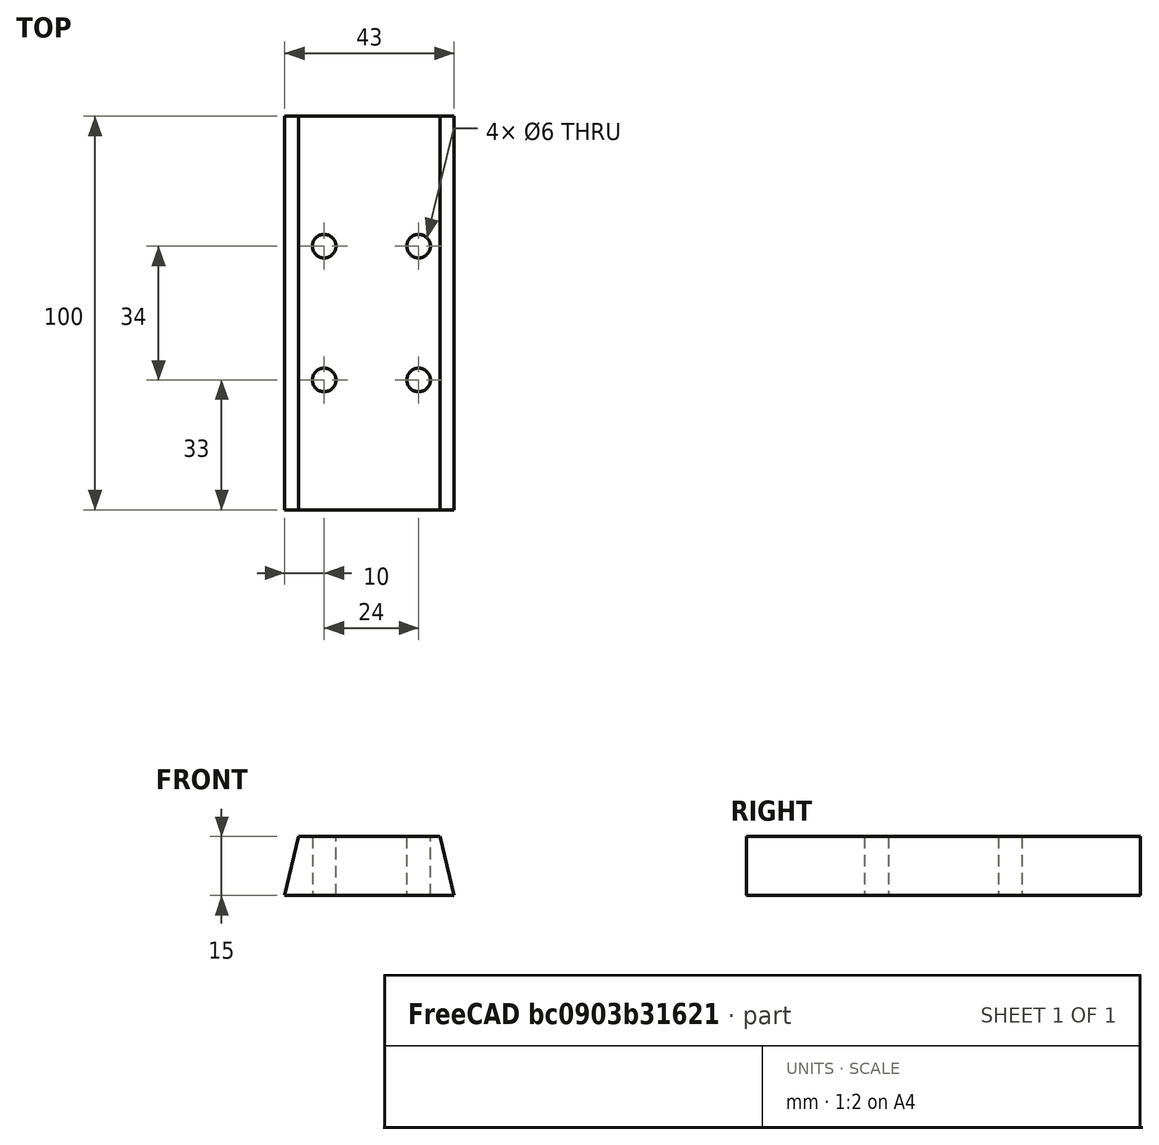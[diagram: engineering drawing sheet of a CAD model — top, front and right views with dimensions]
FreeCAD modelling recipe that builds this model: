
FCSTD DOCUMENT  (FreeCAD 1.0R38641 +678 (Git))
Label: lista k radiu
License: All rights reserved
LicenseURL: https://en.wikipedia.org/wiki/All_rights_reserved
objects: TechDraw::DrawViewDimension×9, Part::Cylinder×4, TechDraw::DrawProjGroupItem×3, Sketcher::SketchObject×1, Part::Extrusion×1, Part::MultiFuse×1, Part::Cut×1, TechDraw::DrawSVGTemplate×1, TechDraw::DrawProjGroup×1, TechDraw::DrawPage×1
note: 22 computed .brp shape members not serialized (recipe doc carries the construction recipe); baked Part::Feature solids carry a one-line shape summary decoded from their .brp

FEATURE [Sketcher::SketchObject] Sketch
  ArcFitTolerance = 1e-06
  FullyConstrained = true
  MakeInternals = false
  Placement = pos=(0,0,0) rot=(1,0,0;1.5708rad)
  sketch-geometry (4):
    g0: LineSegment StartX=0 StartY=0 StartZ=0 EndX=43 EndY=0 EndZ=0
    g1: LineSegment StartX=43 StartY=0 StartZ=0 EndX=39.5 EndY=15 EndZ=0
    g2: LineSegment StartX=39.5 StartY=15 StartZ=0 EndX=3.5 EndY=15 EndZ=0
    g3: LineSegment StartX=3.5 StartY=15 StartZ=0 EndX=0 EndY=0 EndZ=0
  constraints (11):
    c: Coincident(g-1,g0)
    c: PointOnObject(g0,g-1)
    c: Coincident(g0,g1)
    c: Coincident(g1,g2)
    c: Horizontal(g2)
    c: Coincident(g2,g3)
    c: Coincident(g3,g0)
    c: DistanceX(g0,g0) = 43
    c: DistanceX(g2,g2) = 36
    c: DistanceY(g3,g3) = 15
    c: DistanceX(g0,g2) = 3.5
FEATURE [Part::Extrusion] Extrude
  Base = -> Sketch
  Dir = (0,-1,2e-16)
  DirMode = 2
  FaceMakerClass = Part::FaceMakerBullseye
  FaceMakerMode = 3
  LengthFwd = 100
  LengthRev = 0
  Solid = true
  Symmetric = false
FEATURE [Part::Cylinder] Cylinder  label="Válec"
  Angle = 360
  AttacherType = Attacher::AttachEngine3D
  FirstAngle = 0
  Height = 20
  Radius = 3
  SecondAngle = 0
FEATURE [Part::Cylinder] Cylinder001  label="Válec001"
  Angle = 360
  AttacherType = Attacher::AttachEngine3D
  FirstAngle = 0
  Height = 20
  Placement = pos=(0,34,0) rot=(0,1,0;0rad)
  Radius = 3
  SecondAngle = 0
FEATURE [Part::Cylinder] Cylinder002  label="Válec002"
  Angle = 360
  AttacherType = Attacher::AttachEngine3D
  FirstAngle = 0
  Height = 20
  Placement = pos=(24,34,0) rot=(1,1,0;0rad)
  Radius = 3
  SecondAngle = 0
FEATURE [Part::Cylinder] Cylinder003  label="Válec003"
  Angle = 360
  AttacherType = Attacher::AttachEngine3D
  FirstAngle = 0
  Height = 20
  Placement = pos=(24,0,0) rot=(1,0,0;0rad)
  Radius = 3
  SecondAngle = 0
FEATURE [Part::MultiFuse] Fusion
  Placement = pos=(10,-67,0) rot=(1,1,0;0rad)
  Refine = true
  Shapes = -> [Cylinder,Cylinder001,Cylinder002,Cylinder003]
FEATURE [Part::Cut] Cut
  Base = -> Extrude
  Refine = true
  Tool = -> Fusion
FEATURE [TechDraw::DrawSVGTemplate] Template  label="Šablona"
  Height = 210
  Orientation = 1
  Template = /snap/freecad/1634/usr/share/Mod/TechDraw/Templates/Default_Template_A4_Landscape.svg
  Width = 297
FEATURE [TechDraw::DrawProjGroupItem] View  label="Front"
  CoarseView = false
  Direction = (0,-1,0)
  Focus = 100
  HardHidden = false
  IsoCount = 0
  IsoHidden = false
  IsoVisible = false
  LockPosition = true
  Perspective = false
  Rotation = 0
  RotationVector = (1,0,0)
  ScaleType = 2
  ScrubCount = 1
  SeamHidden = false
  SeamVisible = false
  SmoothHidden = false
  SmoothVisible = true
  Source = -> [Cut]
  Type = 0
  X = 0
  XDirection = (1,0,0)
  Y = 0
FEATURE [TechDraw::DrawProjGroupItem] ProjItem001  label="Horní"
  CoarseView = false
  Direction = (0,0,1)
  Focus = 100
  HardHidden = false
  IsoCount = 0
  IsoHidden = false
  IsoVisible = false
  LockPosition = false
  Perspective = false
  Rotation = 0
  RotationVector = (1,0,0)
  ScaleType = 0
  ScrubCount = 1
  SeamHidden = false
  SeamVisible = false
  SmoothHidden = false
  SmoothVisible = true
  Source = -> [Cut]
  Type = 4
  X = 0
  XDirection = (1,0,0)
  Y = -72.5
FEATURE [TechDraw::DrawProjGroupItem] ProjItem  label="FrontTopLeft"
  CoarseView = false
  Direction = (-0.57735,-0.57735,0.57735)
  Focus = 100
  HardHidden = false
  IsoCount = 0
  IsoHidden = false
  IsoVisible = false
  LockPosition = false
  Perspective = false
  Rotation = 0
  RotationVector = (1,0,0)
  ScaleType = 0
  ScrubCount = 1
  SeamHidden = false
  SeamVisible = false
  SmoothHidden = false
  SmoothVisible = true
  Source = -> [Cut]
  Type = 6
  X = 87.0581
  XDirection = (0.707107,-0.707107,0)
  Y = -72.5
FEATURE [TechDraw::DrawProjGroup] ProjGroup
  Anchor = -> View
  AutoDistribute = true
  LockPosition = false
  ProjectionType = 0
  Rotation = 0
  ScaleType = 0
  Source = -> [Cut]
  Views = -> [View,ProjItem001,ProjItem]
  X = 108.341
  Y = 176.328
  spacingX = 15
  spacingY = 15
FEATURE [TechDraw::DrawViewDimension] Dimension  label="Rozměr"
  AngleOverride = false
  Arbitrary = false
  ArbitraryTolerances = false
  BoxCorners = (2) [(-21.5,-7.5,0),(21.5,7.5,0)]
  EqualTolerance = true
  ExtensionAngle = 0
  FormatSpec = %.2w
  FormatSpecOverTolerance = %+.2w
  FormatSpecUnderTolerance = %+.2w
  Inverted = false
  LineAngle = 0
  LockPosition = false
  MeasureType = 1
  OverTolerance = 0
  References2D = -> [View]
  Rotation = 0
  ScaleType = 0
  TheoreticalExact = false
  Type = 1
  UnderTolerance = 0
  X = 0
  Y = 24.9771
FEATURE [TechDraw::DrawViewDimension] Dimension001  label="Rozměr001"
  AngleOverride = false
  Arbitrary = false
  ArbitraryTolerances = false
  BoxCorners = (2) [(-21.5,-7.5,0),(21.5,7.5,0)]
  EqualTolerance = true
  ExtensionAngle = 0
  FormatSpec = %.2w
  FormatSpecOverTolerance = %+.2w
  FormatSpecUnderTolerance = %+.2w
  Inverted = false
  LineAngle = 0
  LockPosition = false
  MeasureType = 1
  OverTolerance = 0
  References2D = -> [View]
  Rotation = 0
  ScaleType = 0
  TheoreticalExact = false
  Type = 1
  UnderTolerance = 0
  X = 0
  Y = -9.05591
FEATURE [TechDraw::DrawViewDimension] Dimension002  label="Rozměr002"
  AngleOverride = false
  Arbitrary = false
  ArbitraryTolerances = false
  BoxCorners = (2) [(-21.5,-7.5,0),(21.5,7.5,0)]
  EqualTolerance = true
  ExtensionAngle = 0
  FormatSpec = %.2w
  FormatSpecOverTolerance = %+.2w
  FormatSpecUnderTolerance = %+.2w
  Inverted = false
  LineAngle = 0
  LockPosition = false
  MeasureType = 1
  OverTolerance = 0
  References2D = -> [View]
  Rotation = 0
  ScaleType = 0
  TheoreticalExact = false
  Type = 2
  UnderTolerance = 0
  X = 28.9959
  Y = 0
FEATURE [TechDraw::DrawViewDimension] Dimension003  label="Rozměr003"
  AngleOverride = false
  Arbitrary = false
  ArbitraryTolerances = false
  BoxCorners = (2) [(-21.5,-50,0),(21.5,50,0)]
  EqualTolerance = true
  ExtensionAngle = 0
  FormatSpec = %.2w
  FormatSpecOverTolerance = %+.2w
  FormatSpecUnderTolerance = %+.2w
  Inverted = false
  LineAngle = 0
  LockPosition = false
  MeasureType = 1
  OverTolerance = 0
  References2D = -> [ProjItem001]
  Rotation = 0
  ScaleType = 0
  TheoreticalExact = false
  Type = 2
  UnderTolerance = 0
  X = -48.0168
  Y = 0
FEATURE [TechDraw::DrawViewDimension] Dimension004  label="Rozměr004"
  AngleOverride = false
  Arbitrary = false
  ArbitraryTolerances = false
  BoxCorners = (2) [(-21.5,-50,0),(21.5,50,0)]
  EqualTolerance = true
  ExtensionAngle = 0
  FormatSpec = M%.2w
  FormatSpecOverTolerance = %+.2w
  FormatSpecUnderTolerance = %+.2w
  Inverted = false
  LineAngle = 0
  LockPosition = false
  MeasureType = 1
  OverTolerance = 0
  References2D = -> [ProjItem001]
  Rotation = 0
  ScaleType = 0
  TheoreticalExact = false
  Type = 5
  UnderTolerance = 0
  X = 6.22352
  Y = -1.4173
FEATURE [TechDraw::DrawViewDimension] Dimension005  label="Rozměr005"
  AngleOverride = false
  Arbitrary = false
  ArbitraryTolerances = false
  BoxCorners = (2) [(-21.5,-50,0),(21.5,50,0)]
  EqualTolerance = true
  ExtensionAngle = 0
  FormatSpec = %.2w
  FormatSpecOverTolerance = %+.2w
  FormatSpecUnderTolerance = %+.2w
  Inverted = false
  LineAngle = 0
  LockPosition = false
  MeasureType = 1
  OverTolerance = 0
  References2D = -> [ProjItem001]
  Rotation = 0
  ScaleType = 0
  TheoreticalExact = false
  Type = 0
  UnderTolerance = 0
  X = 0.5
  Y = 14.6069
FEATURE [TechDraw::DrawViewDimension] Dimension006  label="Rozměr006"
  AngleOverride = false
  Arbitrary = false
  ArbitraryTolerances = false
  BoxCorners = (2) [(-21.5,-50,0),(21.5,50,0)]
  EqualTolerance = true
  ExtensionAngle = 0
  FormatSpec = %.2w
  FormatSpecOverTolerance = %+.2w
  FormatSpecUnderTolerance = %+.2w
  Inverted = false
  LineAngle = 0
  LockPosition = false
  MeasureType = 1
  OverTolerance = 0
  References2D = -> [ProjItem001]
  Rotation = 0
  ScaleType = 0
  TheoreticalExact = false
  Type = 0
  UnderTolerance = 0
  X = -36.8545
  Y = 0
FEATURE [TechDraw::DrawViewDimension] Dimension007  label="Rozměr007"
  AngleOverride = false
  Arbitrary = false
  ArbitraryTolerances = false
  BoxCorners = (2) [(-21.5,-50,0),(21.5,50,0)]
  EqualTolerance = true
  ExtensionAngle = 0
  FormatSpec = %.2w
  FormatSpecOverTolerance = %+.2w
  FormatSpecUnderTolerance = %+.2w
  Inverted = false
  LineAngle = 0
  LockPosition = false
  MeasureType = 1
  OverTolerance = 0
  References2D = -> [ProjItem001]
  Rotation = 0
  ScaleType = 0
  TheoreticalExact = false
  Type = 0
  UnderTolerance = 0
  X = 25.7075
  Y = 28.9348
FEATURE [TechDraw::DrawViewDimension] Dimension008  label="Rozměr008"
  AngleOverride = false
  Arbitrary = false
  ArbitraryTolerances = false
  BoxCorners = (2) [(-21.5,-50,0),(21.5,50,0)]
  EqualTolerance = true
  ExtensionAngle = 0
  FormatSpec = %.2w
  FormatSpecOverTolerance = %+.2w
  FormatSpecUnderTolerance = %+.2w
  Inverted = false
  LineAngle = 0
  LockPosition = false
  MeasureType = 1
  OverTolerance = 0
  References2D = -> [ProjItem001]
  Rotation = 0
  ScaleType = 0
  TheoreticalExact = false
  Type = 0
  UnderTolerance = 0
  X = 5.18443
  Y = 47.2591
FEATURE [TechDraw::DrawPage] Page  label="Stránka"
  KeepUpdated = true
  NextBalloonIndex = 1
  ProjectionType = 0
  Template = -> Template
  Views = -> [ProjGroup,Dimension,Dimension001,Dimension002,Dimension003,Dimension004,Dimension005,Dimension006,Dimension007,Dimension008]
